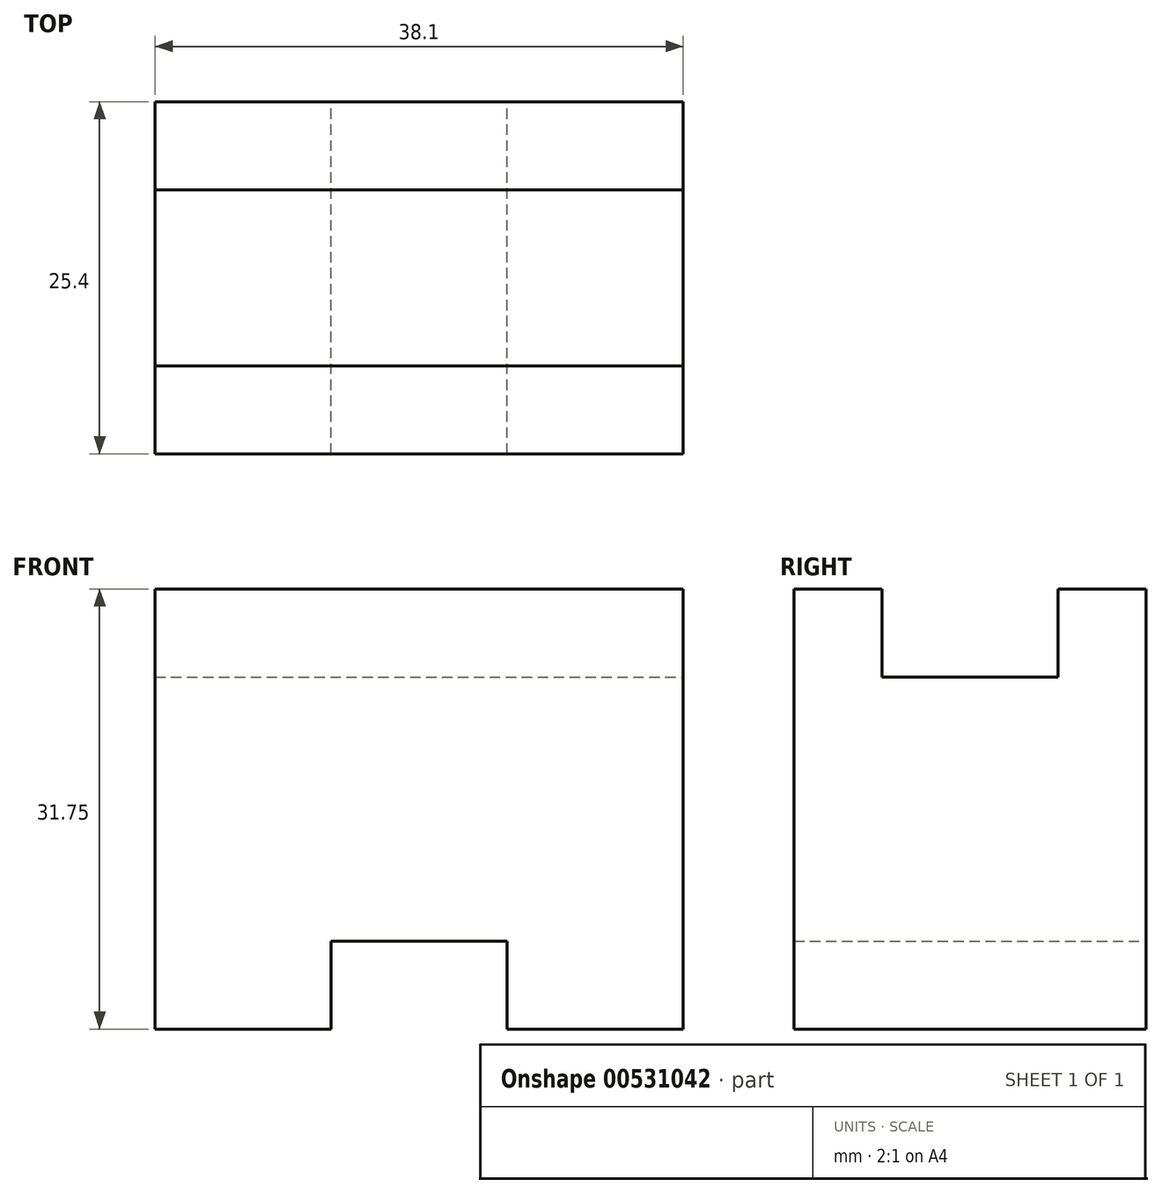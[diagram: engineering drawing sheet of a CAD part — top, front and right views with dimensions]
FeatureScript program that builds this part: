
annotation { "Feature Type Name" : "Feature", "Feature Type Description" : "" }
export const myFeature = defineFeature(function(context is Context, id is Id, definition is map)
    precondition{}
    {
        {
            var Q0;
            Q0=qCreatedBy(makeId("Right.planeOp"),FACE);
            var sketch = newSketch(context, id + "F0", { "sketchPlane" : qUnion([Q0])});
            skLineSegment(sketch, "E0", {"start": v(0, 0) * mm, "end": v(25.4, 0) * mm});
            skLineSegment(sketch, "E1", {"start": v(25.4, 0) * mm, "end": v(25.4, 31.75) * mm});
            skLineSegment(sketch, "E2", {"start": v(25.4, 31.75) * mm, "end": v(0, 31.75) * mm});
            skLineSegment(sketch, "E3", {"start": v(0, 31.75) * mm, "end": v(0, 0) * mm});
            skSolve(sketch);
        }
        {
            var Q0;
            Q0=makeQuery(id+"F0.imprint","IMPRINT",FACE,{"disambiguationData":[TD([[makeQuery(id+"F0.imprint","IMPRINT",EDGE,{"derivedFrom":sQuery(id+"F0.wireOp",EDGE,"E0")}),1.0]])]});
            extrude(context, id + "F1", {"entities" : qUnion([Q0]), "depth" : 38.1 * mm, "offsetDistance" : 25.4 * mm});
        }
        {
            var Q0;
            Q0=makeQuery(id+"F1.opExtrude","SWEPT_FACE",FACE,{"disambiguationData":[OSD([sQuery(id+"F0.wireOp",EDGE,"E2")])]});
            var sketch = newSketch(context, id + "F2", { "sketchPlane" : qUnion([Q0])});
            skLineSegment(sketch, "E4", {"start": v(0, 19.05) * mm, "end": v(38.1, 19.05) * mm});
            skLineSegment(sketch, "E5", {"start": v(0, 6.35) * mm, "end": v(38.1, 6.35) * mm});
            skSolve(sketch);
        }
        {
            var Q0;
            {var subQ0=sQuery(id+"F2.wireOp",EDGE,"E4");Q0=makeQuery(id+"F2.imprint","IMPRINT",FACE,{"disambiguationData":[TD([[makeQuery(id+"F2.imprint","IMPRINT",EDGE,{"derivedFrom":subQ0}),-1.0]])]});}
            extrude(context, id + "F3", {"entities" : qUnion([Q0]), "operationType" : NewBodyOperationType.REMOVE, "oppositeDirection" : true, "depth" : 6.35 * mm, "offsetDistance" : 25.4 * mm});
        }
        {
            var Q0;
            Q0=makeQuery(id+"F1.opExtrude","SWEPT_FACE",FACE,{"disambiguationData":[OSD([sQuery(id+"F0.wireOp",EDGE,"E0")])]});
            var sketch = newSketch(context, id + "F4", { "sketchPlane" : qUnion([Q0])});
            skLineSegment(sketch, "E6", {"start": v(12.7, 0) * mm, "end": v(12.7, -25.4) * mm});
            skLineSegment(sketch, "E7", {"start": v(25.4, 0) * mm, "end": v(25.4, -25.4) * mm});
            skSolve(sketch);
        }
        {
            var Q0;
            {var subQ0=sQuery(id+"F4.wireOp",EDGE,"E6");Q0=makeQuery(id+"F4.imprint","IMPRINT",FACE,{"disambiguationData":[TD([[makeQuery(id+"F4.imprint","IMPRINT",EDGE,{"derivedFrom":subQ0}),1.0]])]});}
            extrude(context, id + "F5", {"entities" : qUnion([Q0]), "operationType" : NewBodyOperationType.REMOVE, "oppositeDirection" : true, "depth" : 6.35 * mm, "offsetDistance" : 25.4 * mm});
        }
    });
